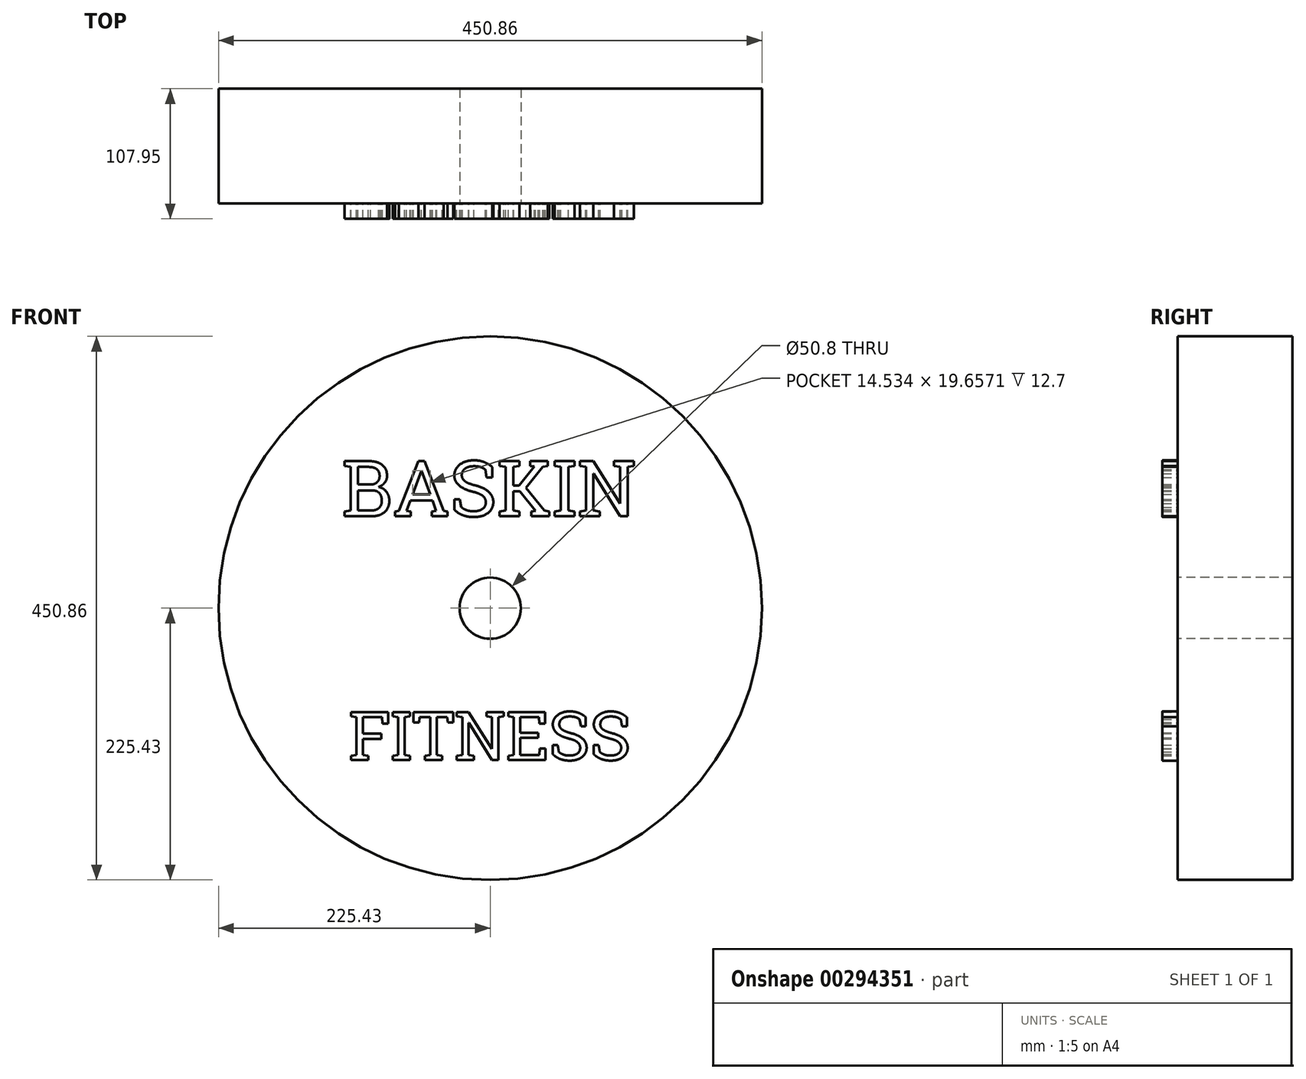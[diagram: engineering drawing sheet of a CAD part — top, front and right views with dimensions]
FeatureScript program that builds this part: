
annotation { "Feature Type Name" : "Feature", "Feature Type Description" : "" }
export const myFeature = defineFeature(function(context is Context, id is Id, definition is map)
    precondition{}
    {
        {
            var Q0;
            Q0=qCreatedBy(makeId("Front.planeOp"),FACE);
            var sketch = newSketch(context, id + "F0", { "sketchPlane" : qUnion([Q0])});
            skCircle(sketch, "E0", {"center": v(0, 0) * mm, "radius": 225.42 * mm});
            skCircle(sketch, "E1", {"center": v(0, 0) * mm, "radius": 25.4 * mm});
            skSolve(sketch);
        }
        {
            var Q0;
            Q0 = qSketchRegion(id + "F0", true);
            extrude(context, id + "F1", {"entities" : qUnion([Q0]), "oppositeDirection" : true, "depth" : 95.25 * mm});
        }
        {
            var Q0;
            Q0=makeQuery(id+"F1.opExtrude","CAP_FACE",FACE,{"disambiguationData":[OSD([sQuery(id+"F0.wireOp",EDGE,"E0"),sQuery(id+"F0.wireOp",EDGE,"E1")])],"isStart":true});
            var sketch = newSketch(context, id + "F2", { "sketchPlane" : qUnion([Q0])});
            skText(sketch, "E2", { "text": "BASKIN", "fontName": "RobotoSlab-Regular.ttf"});
            skText(sketch, "E3", { "text": "FITNESS", "fontName": "RobotoSlab-Regular.ttf"});
            const initialGuessF2  = {"E2": [-0.12315, 0.0762, 1, 0, 0.04638], "E3": [-0.11745, -0.1259, 1, 0, 0.04023]};
            skSetInitialGuess(sketch, initialGuessF2);
            skSolve(sketch);
        }
        {
            var Q0;
            Q0 = qSketchRegion(id + "F2", true);
            extrude(context, id + "F3", {"entities" : qUnion([Q0]), "operationType" : NewBodyOperationType.ADD, "depth" : 12.7 * mm});
        }
    });
